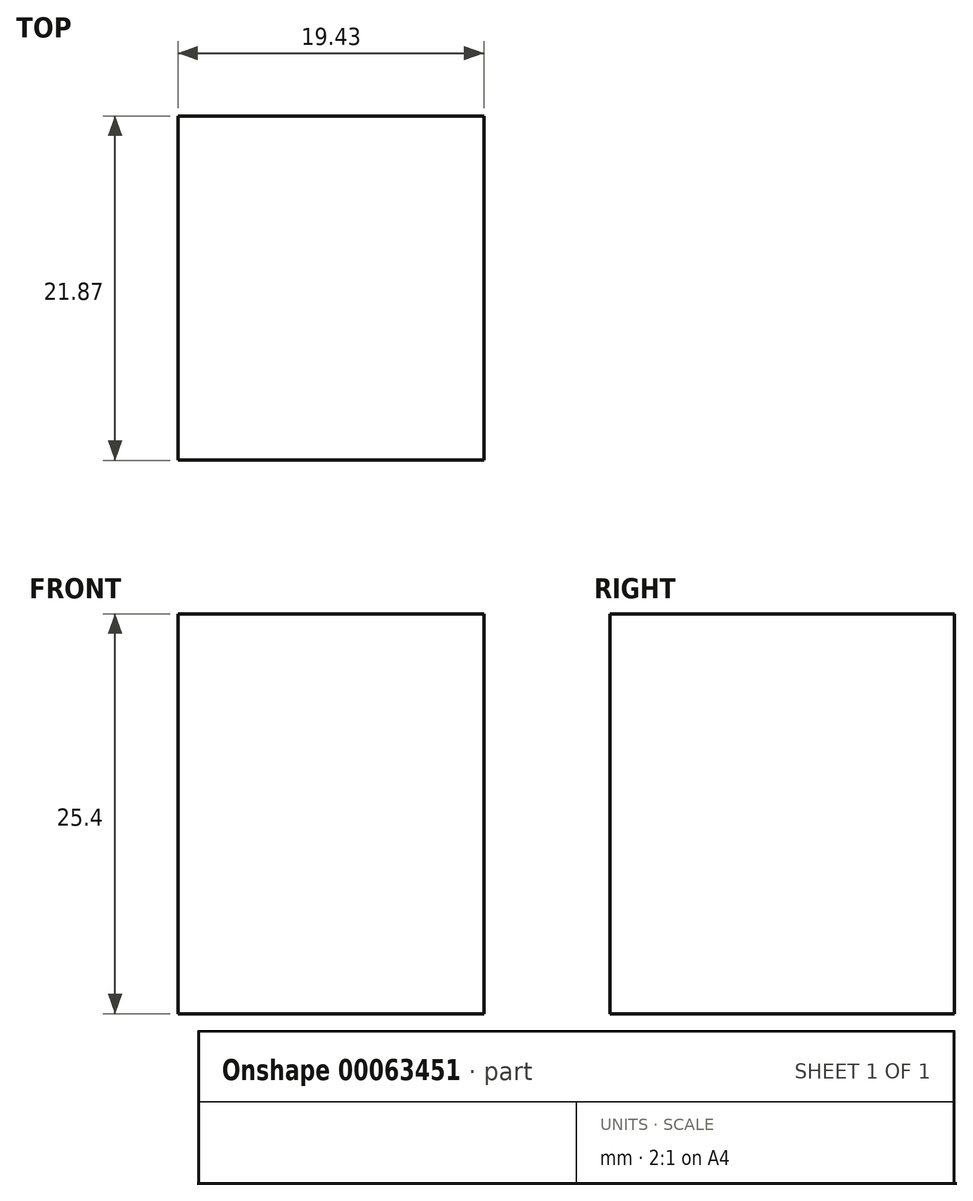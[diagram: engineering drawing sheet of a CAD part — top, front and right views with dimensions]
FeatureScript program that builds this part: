
annotation { "Feature Type Name" : "Feature", "Feature Type Description" : "" }
export const myFeature = defineFeature(function(context is Context, id is Id, definition is map)
    precondition{}
    {
        {
            var Q0;
            Q0=qCreatedBy(makeId("Top.planeOp"),FACE);
            var sketch = newSketch(context, id + "F0", { "sketchPlane" : qUnion([Q0])});
            skLineSegment(sketch, "E0.bottom", {"start": v(-50.71, 40.83) * mm, "end": v(-11.54, 40.83) * mm});
            skLineSegment(sketch, "E0.top", {"start": v(-50.71, 6.83) * mm, "end": v(-11.54, 6.83) * mm});
            skLineSegment(sketch, "E0.left", {"start": v(-50.71, 40.83) * mm, "end": v(-50.71, 6.83) * mm});
            skLineSegment(sketch, "E0.right", {"start": v(-11.54, 40.83) * mm, "end": v(-11.54, 6.83) * mm});
            skSolve(sketch);
        }
        {
            var Q0;
            Q0=makeQuery(id+"F0.imprint","IMPRINT",FACE,{"disambiguationData":[TD([[makeQuery(id+"F0.imprint","IMPRINT",EDGE,{"derivedFrom":sQuery(id+"F0.wireOp",EDGE,"E0.bottom")}),-1.0]])]});
            extrude(context, id + "F1", {"entities" : qUnion([Q0]), "depth" : 25.4 * mm, "hasDraft" : true, "draftAngle" : 0 * degree});
        }
        {
            var Q0;
            Q0=makeQuery(id+"F1.opExtrude","SWEPT_BODY",BODY,{"disambiguationData":[OSD([sQuery(id+"F0.wireOp",EDGE,"E0.bottom"),sQuery(id+"F0.wireOp",EDGE,"E0.top"),sQuery(id+"F0.wireOp",EDGE,"E0.left"),sQuery(id+"F0.wireOp",EDGE,"E0.right")])]});
            deleteBodies(context, id + "F2", {"entities" : qUnion([Q0])});
        }
        {
            var Q0;
            Q0=qCreatedBy(makeId("Top.planeOp"),FACE);
            var sketch = newSketch(context, id + "F3", { "sketchPlane" : qUnion([Q0])});
            skLineSegment(sketch, "E1.bottom", {"start": v(-19.43, -29.6) * mm, "end": v(0, -29.6) * mm});
            skLineSegment(sketch, "E1.top", {"start": v(-19.43, -7.74) * mm, "end": v(0, -7.74) * mm});
            skLineSegment(sketch, "E1.left", {"start": v(-19.43, -29.6) * mm, "end": v(-19.43, -7.74) * mm});
            skLineSegment(sketch, "E1.right", {"start": v(0, -29.6) * mm, "end": v(0, -7.74) * mm});
            skSolve(sketch);
        }
        {
            var Q0;
            Q0=makeQuery(id+"F3.imprint","IMPRINT",FACE,{"disambiguationData":[TD([[makeQuery(id+"F3.imprint","IMPRINT",EDGE,{"derivedFrom":sQuery(id+"F3.wireOp",EDGE,"E1.bottom")}),1.0]])]});
            extrude(context, id + "F4", {"entities" : qUnion([Q0]), "depth" : 25.4 * mm, "hasDraft" : true, "draftAngle" : 0 * degree});
        }
    });
